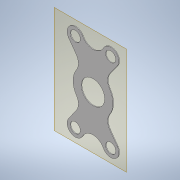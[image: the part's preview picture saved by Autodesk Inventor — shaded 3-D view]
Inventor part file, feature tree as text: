
AUTODESK INVENTOR PART (.ipt)
format: ipt  version: 2022 (Build 260153000, 153)  size: 154,624 bytes
history: native  units: mm
features: other x3, reference x2, plane x1, extrude x1, sketch x1
ambient origin geometry x8: Origin, YZ Plane, XZ Plane, XY Plane, X Axis, Y Axis, Z Axis, Center Point
bodies: Solid1 (feature_tree)
feature tree (8):
  plane  "Work Plane1"
  extrude  "Extrusion1"  Depth=0.3mm TaperAngle=0.0deg
  sketch  "Sketch1"  dims[d0=0.3mm d1=0.3mm d2=0.0mm d3=0.2mm]
  reference  "Reference1"
  reference  "Reference2"
  other  "<userpath>\OneDrive - Imperial College London\ROBOICP MK2\solids feeder assembly.iam"
  other  "solids feeder assembly.iam"
  other  "shaft encap lid:1"
